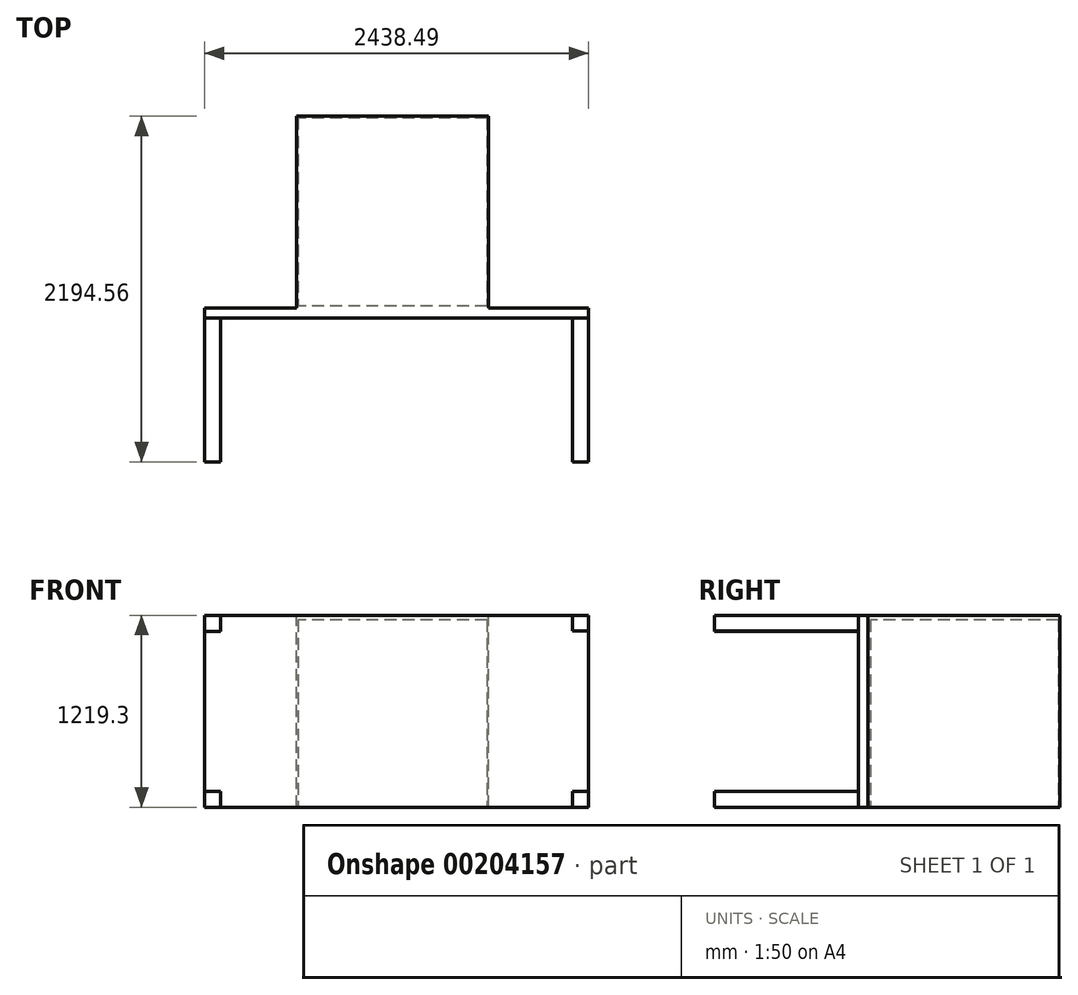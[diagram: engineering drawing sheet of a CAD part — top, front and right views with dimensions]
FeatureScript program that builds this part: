
annotation { "Feature Type Name" : "Feature", "Feature Type Description" : "" }
export const myFeature = defineFeature(function(context is Context, id is Id, definition is map)
    precondition{}
    {
        {
            var Q0;
            Q0=qCreatedBy(makeId("Front.planeOp"),FACE);
            var sketch = newSketch(context, id + "F0", { "sketchPlane" : qUnion([Q0])});
            skLineSegment(sketch, "E0.bottom", {"start": v(0, 0) * mm, "end": v(2438.4, 0) * mm});
            skLineSegment(sketch, "E0.top", {"start": v(0, 1219.2) * mm, "end": v(2438.4, 1219.2) * mm});
            skLineSegment(sketch, "E0.left", {"start": v(0, 0) * mm, "end": v(0, 1219.2) * mm});
            skLineSegment(sketch, "E0.right", {"start": v(2438.4, 0) * mm, "end": v(2438.4, 1219.2) * mm});
            skSolve(sketch);
        }
        {
            var Q0;
            Q0=makeQuery(id+"F0.imprint","IMPRINT",FACE,{"disambiguationData":[TD([[makeQuery(id+"F0.imprint","IMPRINT",EDGE,{"derivedFrom":sQuery(id+"F0.wireOp",EDGE,"E0.bottom")}),1.0]])]});
            extrude(context, id + "F1", {"entities" : qUnion([Q0]), "depth" : 60.96 * mm});
        }
        {
            var Q0;
            Q0=makeQuery(id+"F1.opExtrude","CAP_FACE",FACE,{"disambiguationData":[OSD([sQuery(id+"F0.wireOp",EDGE,"E0.bottom"),sQuery(id+"F0.wireOp",EDGE,"E0.top"),sQuery(id+"F0.wireOp",EDGE,"E0.left"),sQuery(id+"F0.wireOp",EDGE,"E0.right")])],"isStart":false});
            var sketch = newSketch(context, id + "F2", { "sketchPlane" : qUnion([Q0])});
            skSolve(sketch);
        }
        {
            var Q0;
            Q0=makeQuery(id+"F2.imprint","IMPRINT",FACE,{"disambiguationData":[TD([[makeQuery(id+"F2.imprint","IMPRINT",EDGE,{"derivedFrom":makeQuery(id+"F1.opExtrude","CAP_EDGE",EDGE,{"disambiguationData":[OSD([sQuery(id+"F0.wireOp",EDGE,"E0.bottom")])],"isStart":false})}),1.0]])]});
            var sketch = newSketch(context, id + "F3", { "sketchPlane" : qUnion([Q0])});
            skLineSegment(sketch, "E1.bottom", {"start": v(0, 0) * mm, "end": v(100.58, 0) * mm});
            skLineSegment(sketch, "E1.top", {"start": v(0, 100.58) * mm, "end": v(100.58, 100.58) * mm});
            skLineSegment(sketch, "E1.left", {"start": v(0, 0) * mm, "end": v(0, 100.58) * mm});
            skLineSegment(sketch, "E1.right", {"start": v(100.58, 0) * mm, "end": v(100.58, 100.58) * mm});
            skLineSegment(sketch, "E2.bottom", {"start": v(0, 1217.6) * mm, "end": v(100.58, 1217.6) * mm});
            skLineSegment(sketch, "E2.top", {"start": v(0, 1117.01) * mm, "end": v(100.58, 1117.01) * mm});
            skLineSegment(sketch, "E2.left", {"start": v(0, 1217.6) * mm, "end": v(0, 1117.01) * mm});
            skLineSegment(sketch, "E2.right", {"start": v(100.58, 1217.6) * mm, "end": v(100.58, 1117.01) * mm});
            skLineSegment(sketch, "E3.bottom", {"start": v(2337.8, 1219.22) * mm, "end": v(2438.38, 1219.22) * mm});
            skLineSegment(sketch, "E3.top", {"start": v(2337.8, 1118.64) * mm, "end": v(2438.38, 1118.64) * mm});
            skLineSegment(sketch, "E3.left", {"start": v(2337.8, 1219.22) * mm, "end": v(2337.8, 1118.64) * mm});
            skLineSegment(sketch, "E3.right", {"start": v(2438.38, 1219.22) * mm, "end": v(2438.38, 1118.64) * mm});
            skLineSegment(sketch, "E4.bottom", {"start": v(2337.9, 100.5) * mm, "end": v(2438.49, 100.5) * mm});
            skLineSegment(sketch, "E4.top", {"start": v(2337.9, -0.08) * mm, "end": v(2438.49, -0.08) * mm});
            skLineSegment(sketch, "E4.left", {"start": v(2337.9, 100.5) * mm, "end": v(2337.9, -0.08) * mm});
            skLineSegment(sketch, "E4.right", {"start": v(2438.49, 100.5) * mm, "end": v(2438.49, -0.08) * mm});
            skSolve(sketch);
        }
        {
            var Q0;
            Q0 = qSketchRegion(id + "F3", true);
            extrude(context, id + "F4", {"entities" : qUnion([Q0]), "operationType" : NewBodyOperationType.ADD, "depth" : 914.4 * mm});
        }
        {
            var Q0;
            Q0=makeQuery(id+"F1.opExtrude","CAP_FACE",FACE,{"disambiguationData":[OSD([sQuery(id+"F0.wireOp",EDGE,"E0.bottom"),sQuery(id+"F0.wireOp",EDGE,"E0.top"),sQuery(id+"F0.wireOp",EDGE,"E0.left"),sQuery(id+"F0.wireOp",EDGE,"E0.right")])],"isStart":true});
            var sketch = newSketch(context, id + "F5", { "sketchPlane" : qUnion([Q0])});
            skLineSegment(sketch, "E5.bottom", {"start": v(-1802.32, 0) * mm, "end": v(-583.12, 0) * mm});
            skLineSegment(sketch, "E5.top", {"start": v(-1802.32, 1219.2) * mm, "end": v(-583.12, 1219.2) * mm});
            skLineSegment(sketch, "E5.left", {"start": v(-1802.32, 0) * mm, "end": v(-1802.32, 1219.2) * mm});
            skLineSegment(sketch, "E5.right", {"start": v(-583.12, 0) * mm, "end": v(-583.12, 1219.2) * mm});
            skSolve(sketch);
        }
        {
            var Q0;
            Q0=makeQuery(id+"F5.imprint","IMPRINT",FACE,{"disambiguationData":[TD([[makeQuery(id+"F5.imprint","IMPRINT",EDGE,{"derivedFrom":sQuery(id+"F5.wireOp",EDGE,"E5.bottom")}),1.0]])]});
            var Q1;
            Q1=makeQuery(id+"F5.imprint","IMPRINT",FACE,{"disambiguationData":[TD([[makeQuery(id+"F5.imprint","IMPRINT",EDGE,{"derivedFrom":sQuery(id+"F5.wireOp",EDGE,"E5.bottom")}),-1.0]])]});
            extrude(context, id + "F6", {"entities" : qUnion([Q0, Q1]), "operationType" : NewBodyOperationType.ADD, "depth" : 1219.2 * mm});
        }
        {
            var Q0;
            Q0=makeQuery(id+"F6.boolean.opBoolean","MERGE",FACE,{"derivedFrom":[makeQuery(id+"F4.boolean.opBoolean","MERGE",FACE,{"derivedFrom":[makeQuery(id+"F1.opExtrude","SWEPT_FACE",FACE,{"disambiguationData":[OSD([sQuery(id+"F0.wireOp",EDGE,"E0.bottom")])]}),makeQuery(id+"F4.opExtrude","SWEPT_FACE",FACE,{"disambiguationData":[OSD([sQuery(id+"F3.wireOp",EDGE,"E1.bottom")])]})]}),makeQuery(id+"F6.opExtrude","SWEPT_FACE",FACE,{"disambiguationData":[OSD([sQuery(id+"F5.wireOp",EDGE,"E5.bottom")])]})]});
            var sketch = newSketch(context, id + "F7", { "sketchPlane" : qUnion([Q0])});
            skLineSegment(sketch, "E6.bottom", {"start": v(1792.88, -1208.63) * mm, "end": v(593.36, -1208.63) * mm});
            skLineSegment(sketch, "E6.top", {"start": v(1792.88, -14.36) * mm, "end": v(593.36, -14.36) * mm});
            skLineSegment(sketch, "E6.left", {"start": v(1792.88, -1208.63) * mm, "end": v(1792.88, -14.36) * mm});
            skLineSegment(sketch, "E6.right", {"start": v(593.36, -1208.63) * mm, "end": v(593.36, -14.36) * mm});
            skSolve(sketch);
        }
        {
            var Q0;
            Q0=makeQuery(id+"F7.imprint","IMPRINT",FACE,{"disambiguationData":[TD([[makeQuery(id+"F7.imprint","IMPRINT",EDGE,{"derivedFrom":sQuery(id+"F7.wireOp",EDGE,"E6.bottom")}),-1.0]])]});
            extrude(context, id + "F8", {"entities" : qUnion([Q0]), "operationType" : NewBodyOperationType.REMOVE, "oppositeDirection" : true, "depth" : 1188.72 * mm});
        }
    });
